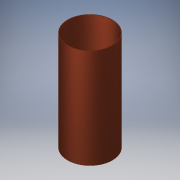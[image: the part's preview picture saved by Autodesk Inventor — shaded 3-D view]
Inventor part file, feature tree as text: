
AUTODESK INVENTOR PART (.ipt)
format: ipt  version: 2018 (Build 220112000, 112)  size: 99,840 bytes
history: native  units: in
note: dims shown in document units (in); Inventor stores cm internally (conversion verified against a paired STEP export)
features: extrude x1, sketch x1
ambient origin geometry x8: Origin, YZ Plane, XZ Plane, XY Plane, X Axis, Y Axis, Z Axis, Center Point
bodies: Solid1 (feature_tree)
feature tree (2):
  extrude  "Extrusion1"  Depth=17.5in
  sketch  "Sketch1"  dims[d0=7.75in d1=0.06in d2=17.5in d3=0.0in]
